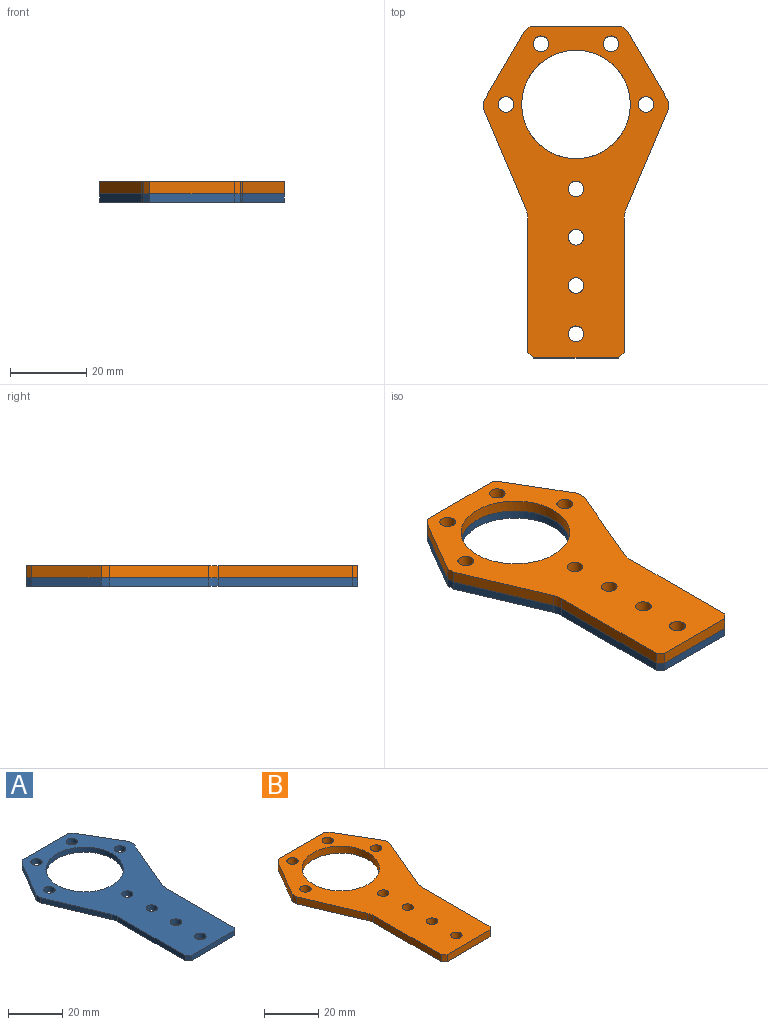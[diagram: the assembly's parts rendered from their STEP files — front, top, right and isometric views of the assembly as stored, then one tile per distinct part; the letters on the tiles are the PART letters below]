
ASSEMBLY  parts=2 mates=1
PART A: 27 faces, bbox 48.6x87.3x2.3 mm
  f0: cylinder r=2.07mm len=4.14mm, axis (0,0,-1), area 29.7mm2, adj f9,f10
  f1: cylinder r=2.07mm len=4.14mm, axis (0,0,-1), area 29.7mm2, adj f9,f10
  f2: cylinder r=2.07mm len=4.14mm, axis (0,0,-1), area 29.7mm2, adj f9,f10
  f3: cylinder r=2.07mm len=4.14mm, axis (0,0,-1), area 29.7mm2, adj f9,f10
  f4: cylinder r=2.07mm len=4.14mm, axis (0,0,-1), area 29.7mm2, adj f9,f10
  f5: cylinder r=2.07mm len=4.14mm, axis (0,0,-1), area 29.7mm2, adj f9,f10
  f6: cylinder r=2.07mm len=4.14mm, axis (0,0,-1), area 29.7mm2, adj f9,f10
  f7: cylinder r=2.07mm len=4.14mm, axis (0,0,-1), area 29.7mm2, adj f9,f10
  f8: cylinder r=14.29mm len=28.58mm, axis (0,0,-1), area 205.2mm2, adj f9,f10
  f9: plane 87.31x48.56mm, normal (0,0,1), area 2060.7mm2, adj f0,f1,f2,f3,f4,f5,f6,f7
  f10: plane 87.31x48.56mm, normal (0,0,-1), area 2060.7mm2, adj f0,f1,f2,f3,f4,f5,f6,f7
  f11: plane 22.35x2.29mm, normal (0,-1,0), area 51.1mm2, adj f9,f10,f25,f26
  f12: plane 35.28x2.29mm, normal (-1,0,0), area 80.7mm2, adj f9,f10,f20,f26
  f13: plane 35.28x2.29mm, normal (1,0,0), area 80.7mm2, adj f9,f10,f19,f25
  f14: plane 18.21x10.69mm, normal (-0.86,0.51,0), area 48.3mm2, adj f9,f10,f21,f24
  f15: plane 26.13x11.08mm, normal (-0.92,-0.39,0), area 64.9mm2, adj f9,f10,f20,f24
  f16: plane 18.21x10.69mm, normal (0.86,0.51,0), area 48.3mm2, adj f9,f10,f22,f23
  f17: plane 26.13x11.08mm, normal (0.92,-0.39,0), area 64.9mm2, adj f9,f10,f19,f23
  f18: plane 24.14x2.29mm, normal (0,1,0), area 55.2mm2, adj f9,f10,f21,f22
  f19: cylinder r=6.35mm len=2.48mm, axis (0,0,1), area 5.8mm2, adj f9,f10,f13,f17
  f20: cylinder r=6.35mm len=2.48mm, axis (0,0,1), area 5.8mm2, adj f9,f10,f12,f15
  f21: plane 2.29x1.53mm, normal (-0.71,0.71,0), area 4.9mm2, adj f9,f10,f14,f18
  f22: plane 2.29x1.53mm, normal (0.71,0.71,0), area 4.9mm2, adj f9,f10,f16,f18
  f23: plane 2.29x2.16mm, normal (1,0,0), area 4.9mm2, adj f9,f10,f16,f17
  f24: plane 2.29x2.16mm, normal (-1,0,0), area 4.9mm2, adj f9,f10,f14,f15
  f25: plane 2.29x1.53mm, normal (0.71,-0.71,0), area 4.9mm2, adj f9,f10,f11,f13
  f26: plane 2.29x1.53mm, normal (-0.71,-0.71,0), area 4.9mm2, adj f9,f10,f11,f12
PART B: 27 faces, bbox 48.6x87.3x3.2 mm
  f0: plane 24.14x3.18mm, normal (0,1,0), area 76.6mm2, adj f1,f2,f4,f18
  f1: plane 87.31x48.56mm, normal (0,0,-1), area 2060.7mm2, adj f0,f3,f4,f5,f6,f7,f8,f9
  f2: plane 87.31x48.56mm, normal (0,0,1), area 2060.7mm2, adj f0,f3,f4,f5,f6,f7,f8,f9
  f3: cylinder r=2.07mm len=4.14mm, axis (0,0,-1), area 41.3mm2, adj f1,f2
  f4: plane 3.18x1.53mm, normal (-0.71,0.71,0), area 6.9mm2, adj f0,f1,f2,f5
  f5: plane 18.21x10.69mm, normal (-0.86,0.51,0), area 67mm2, adj f1,f2,f4,f6
  f6: plane 3.18x2.16mm, normal (-1,0,0), area 6.9mm2, adj f1,f2,f5,f7
  f7: plane 26.13x11.08mm, normal (-0.92,-0.39,0), area 90.1mm2, adj f1,f2,f6,f8
  f8: cylinder r=6.35mm len=3.18mm, axis (0,0,-1), area 8.1mm2, adj f1,f2,f7,f9
  f9: plane 35.28x3.18mm, normal (-1,0,0), area 112mm2, adj f1,f2,f8,f10
  f10: plane 3.18x1.53mm, normal (-0.71,-0.71,0), area 6.9mm2, adj f1,f2,f9,f11
  f11: plane 22.35x3.18mm, normal (0,-1,0), area 71mm2, adj f1,f2,f10,f12
  f12: plane 3.18x1.53mm, normal (0.71,-0.71,0), area 6.9mm2, adj f1,f2,f11,f13
  f13: plane 35.28x3.18mm, normal (1,0,0), area 112mm2, adj f1,f2,f12,f14
  f14: cylinder r=6.35mm len=3.18mm, axis (0,0,-1), area 8.1mm2, adj f1,f2,f13,f15
  f15: plane 26.13x11.08mm, normal (0.92,-0.39,0), area 90.1mm2, adj f1,f2,f14,f16
  f16: plane 3.18x2.16mm, normal (1,0,0), area 6.9mm2, adj f1,f2,f15,f17
  f17: plane 18.21x10.69mm, normal (0.86,0.51,0), area 67mm2, adj f1,f2,f16,f18
  f18: plane 3.18x1.53mm, normal (0.71,0.71,0), area 6.9mm2, adj f0,f1,f2,f17
  f19: cylinder r=2.07mm len=4.14mm, axis (0,0,-1), area 41.3mm2, adj f1,f2
  f20: cylinder r=2.07mm len=4.14mm, axis (0,0,-1), area 41.3mm2, adj f1,f2
  f21: cylinder r=2.07mm len=4.14mm, axis (0,0,-1), area 41.3mm2, adj f1,f2
  f22: cylinder r=14.29mm len=28.58mm, axis (0,0,-1), area 285mm2, adj f1,f2
  f23: cylinder r=2.07mm len=4.14mm, axis (0,0,-1), area 41.3mm2, adj f1,f2
  f24: cylinder r=2.07mm len=4.14mm, axis (0,0,-1), area 41.3mm2, adj f1,f2
  f25: cylinder r=2.07mm len=4.14mm, axis (0,0,-1), area 41.3mm2, adj f1,f2
  f26: cylinder r=2.07mm len=4.14mm, axis (0,0,-1), area 41.3mm2, adj f1,f2
PLACE A t=(28.65,50.62,11.54)mm
PLACE B t=(3.25,-17.64,13.82)mm
MATE fastened A.f9 <-> B.f1  axis (0,0,1) through (28.65,71.26,13.82)mm
